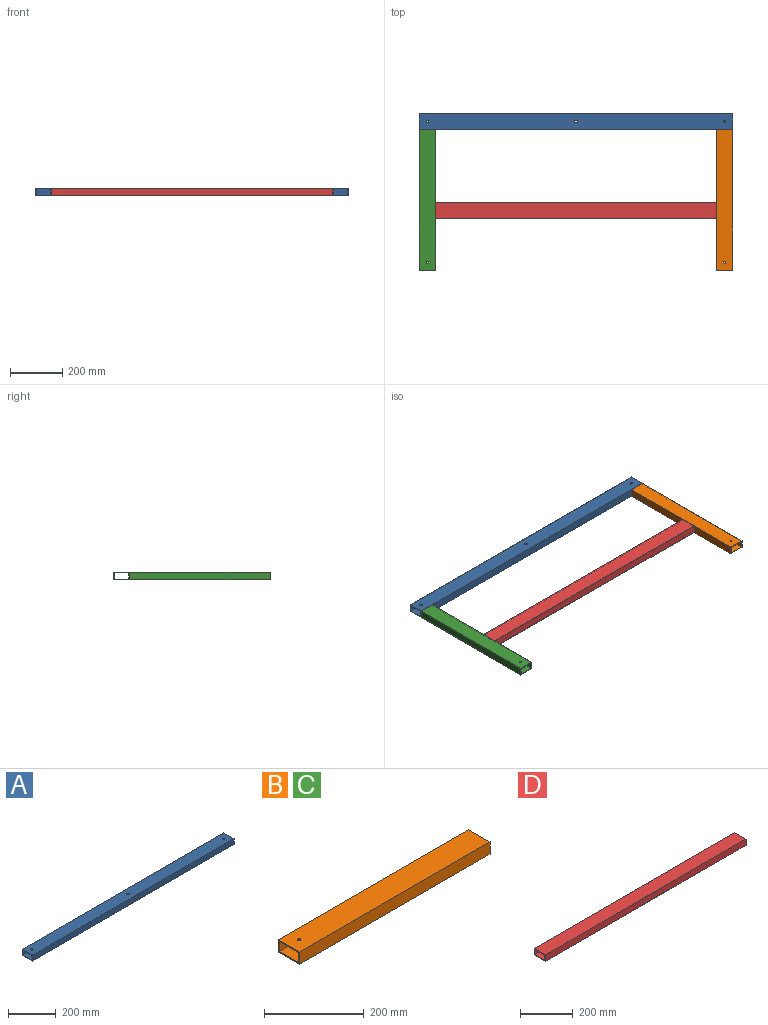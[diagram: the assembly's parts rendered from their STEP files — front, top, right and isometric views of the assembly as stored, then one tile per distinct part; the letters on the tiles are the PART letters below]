
ASSEMBLY  parts=4 mates=3
PART A: 16 faces, bbox 1200x60x30 mm
  f0: plane 1200x30mm, normal (0,-1,0), area 36000mm2, adj f2,f3,f4,f9
  f1: plane 1200x30mm, normal (0,1,0), area 36000mm2, adj f2,f3,f4,f9
  f2: plane 60x30mm, normal (-1,0,0), area 504mm2, adj f0,f1,f3,f4,f5,f6,f7,f8
  f3: plane 1200x60mm, normal (0,0,1), area 71764.4mm2, adj f0,f1,f2,f9,f10,f11,f12
  f4: plane 1200x60mm, normal (0,0,-1), area 70670.7mm2, adj f0,f1,f2,f9,f13,f14,f15
  f5: plane 1200x54mm, normal (0,0,1), area 63470.7mm2, adj f2,f6,f8,f9,f13,f14,f15
  f6: plane 1200x24mm, normal (0,1,0), area 28800mm2, adj f2,f5,f7,f9
  f7: plane 1200x54mm, normal (0,0,-1), area 64564.4mm2, adj f2,f6,f8,f9,f10,f11,f12
  f8: plane 1200x24mm, normal (0,-1,0), area 28800mm2, adj f2,f5,f7,f9
  f9: plane 60x30mm, normal (1,0,0), area 504mm2, adj f0,f1,f3,f4,f5,f6,f7,f8
  f10: cylinder r=5mm len=10mm, axis (0,0,1), area 94.2mm2, adj f3,f7
  f11: cylinder r=5mm len=10mm, axis (0,0,1), area 94.2mm2, adj f3,f7
  f12: cylinder r=5mm len=10mm, axis (0,0,1), area 94.2mm2, adj f3,f7
  f13: cylinder r=20mm len=40mm, axis (0,0,-1), area 377mm2, adj f4,f5
  f14: cylinder r=3.4mm len=6.8mm, axis (0,0,-1), area 64.1mm2, adj f4,f5
  f15: cylinder r=3.4mm len=6.8mm, axis (0,0,-1), area 64.1mm2, adj f4,f5
PART B: 12 faces, bbox 540x60x30 mm
  f0: plane 540x30mm, normal (0,1,0), area 16200mm2, adj f1,f2,f8,f9
  f1: plane 540x60mm, normal (0,0,1), area 32363.7mm2, adj f0,f7,f8,f9,f10
  f2: plane 540x60mm, normal (0,0,-1), area 32363.7mm2, adj f0,f7,f8,f9,f11
  f3: plane 540x54mm, normal (0,0,1), area 29123.7mm2, adj f4,f6,f8,f9,f11
  f4: plane 540x24mm, normal (0,1,0), area 12960mm2, adj f3,f5,f8,f9
  f5: plane 540x54mm, normal (0,0,-1), area 29123.7mm2, adj f4,f6,f8,f9,f10
  f6: plane 540x24mm, normal (0,-1,0), area 12960mm2, adj f3,f5,f8,f9
  f7: plane 540x30mm, normal (0,-1,0), area 16200mm2, adj f1,f2,f8,f9
  f8: plane 60x30mm, normal (1,0,0), area 504mm2, adj f0,f1,f2,f3,f4,f5,f6,f7
  f9: plane 60x30mm, normal (-1,0,0), area 504mm2, adj f0,f1,f2,f3,f4,f5,f6,f7
  f10: cylinder r=3.4mm len=6.8mm, axis (0,0,1), area 64.1mm2, adj f1,f5
  f11: cylinder r=3.4mm len=6.8mm, axis (0,0,1), area 64.1mm2, adj f2,f3
PART C: same geometry as B
PART D: 10 faces, bbox 1080x60x30 mm
  f0: plane 1080x30mm, normal (0,-1,0), area 32400mm2, adj f1,f3,f4,f5
  f1: plane 60x30mm, normal (1,0,0), area 504mm2, adj f0,f2,f4,f5,f6,f7,f8,f9
  f2: plane 1080x30mm, normal (0,1,0), area 32400mm2, adj f1,f3,f4,f5
  f3: plane 60x30mm, normal (-1,0,0), area 504mm2, adj f0,f2,f4,f5,f6,f7,f8,f9
  f4: plane 1080x60mm, normal (0,0,1), area 64800mm2, adj f0,f1,f2,f3
  f5: plane 1080x60mm, normal (0,0,-1), area 64800mm2, adj f0,f1,f2,f3
  f6: plane 1080x54mm, normal (0,0,1), area 58320mm2, adj f1,f3,f7,f9
  f7: plane 1080x24mm, normal (0,1,0), area 25920mm2, adj f1,f3,f6,f8
  f8: plane 1080x54mm, normal (0,0,-1), area 58320mm2, adj f1,f3,f7,f9
  f9: plane 1080x24mm, normal (0,-1,0), area 25920mm2, adj f1,f3,f6,f8
PLACE A t=(-556.27,447.6,-15)mm
PLACE B rot(axis=(0,0,1),90deg) t=(152.4,-1696.27,-168)mm
PLACE C rot(axis=(0,0,1),90deg) t=(-987.6,-1696.27,-168)mm
PLACE D t=(-496.27,-346.4,-15)mm
MATE fastened A.f3 <-> C.f1  axis (0,0,1) through (-600,0,15)mm
MATE planar D.f4 <-> A.f10  axis (0,0,1) through (0,-310,15)mm
MATE fastened B.f1 <-> A.f3  axis (0,0,1) through (600,0,15)mm
